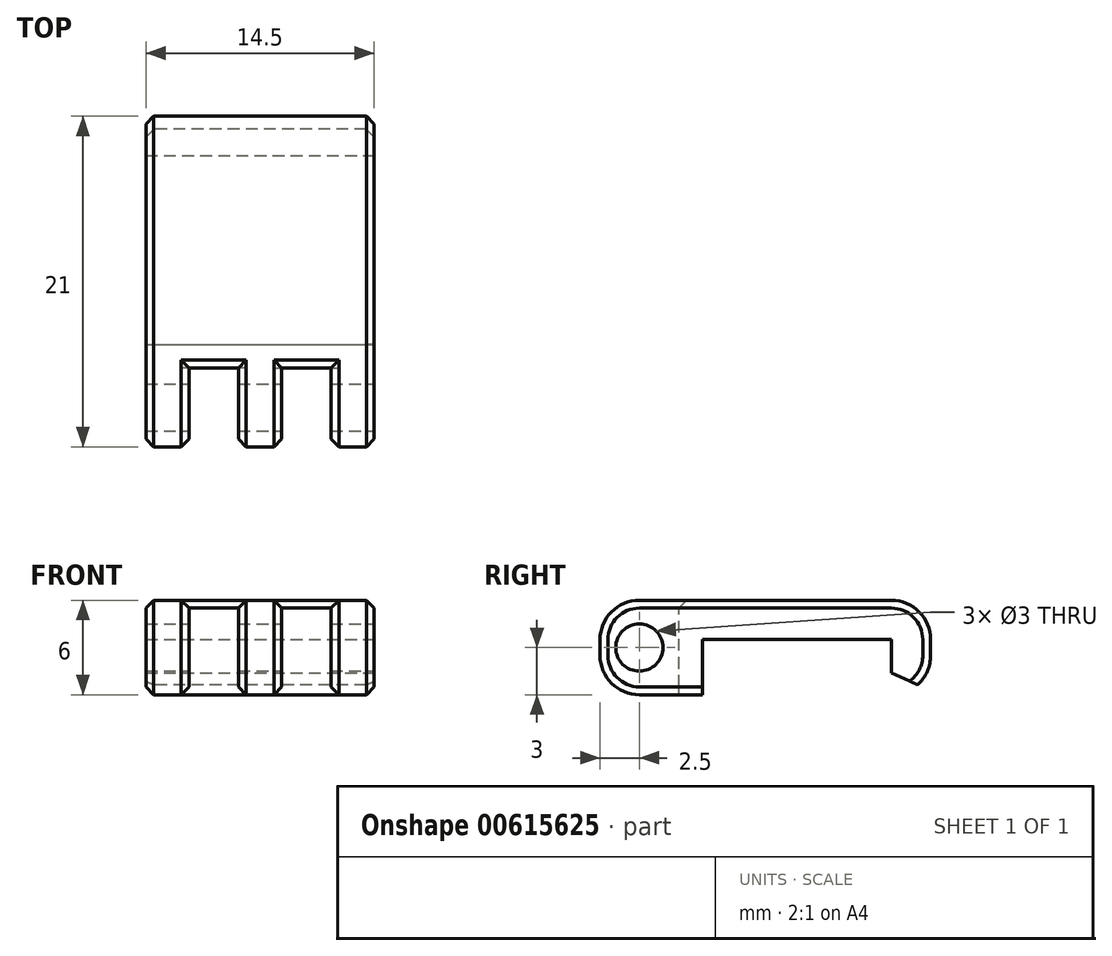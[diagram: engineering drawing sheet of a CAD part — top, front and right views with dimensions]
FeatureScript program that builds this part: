
annotation { "Feature Type Name" : "Feature", "Feature Type Description" : "" }
export const myFeature = defineFeature(function(context is Context, id is Id, definition is map)
    precondition{}
    {
        {
            var Q0;
            Q0=qCreatedBy(makeId("Top.planeOp"),FACE);
            var sketch = newSketch(context, id + "F0", { "sketchPlane" : qUnion([Q0])});
            skLineSegment(sketch, "E0.bottom", {"start": v(-7.25, 10.5) * mm, "end": v(7.25, 10.5) * mm});
            skLineSegment(sketch, "E0.top", {"start": v(-7.25, -10.5) * mm, "end": v(7.25, -10.5) * mm});
            skLineSegment(sketch, "E0.left", {"start": v(-7.25, 10.5) * mm, "end": v(-7.25, -10.5) * mm});
            skLineSegment(sketch, "E0.right", {"start": v(7.25, 10.5) * mm, "end": v(7.25, -10.5) * mm});
            skSolve(sketch);
        }
        {
            var Q0;
            Q0=qSketchRegion(id+"F0",true);
            extrude(context, id + "F1", {"entities" : qUnion([Q0]), "endBound" : BoundingType.SYMMETRIC, "depth" : 6 * mm, "offsetDistance" : 25 * mm});
        }
        {
            var Q0;
            Q0=qCreatedBy(makeId("Right.planeOp"),FACE);
            var sketch = newSketch(context, id + "F2", { "sketchPlane" : qUnion([Q0])});
            skCircle(sketch, "E1", {"center": v(-8, 0) * mm, "radius": 1.5 * mm});
            skSolve(sketch);
        }
        {
            var Q0;
            Q0=qSketchRegion(id+"F2",true);
            extrude(context, id + "F3", {"entities" : qUnion([Q0]), "operationType" : NewBodyOperationType.REMOVE, "endBound" : BoundingType.SYMMETRIC, "oppositeDirection" : true, "depth" : 50 * mm, "offsetDistance" : 25 * mm});
        }
        {
            var Q0;
            Q0=makeQuery(id+"F1.opExtrude","CAP_EDGE",EDGE,{"disambiguationData":[OSD([sQuery(id+"F0.wireOp",EDGE,"E0.top")])],"isStart":false});
            var Q1;
            Q1=makeQuery(id+"F1.opExtrude","CAP_EDGE",EDGE,{"disambiguationData":[OSD([sQuery(id+"F0.wireOp",EDGE,"E0.top")])],"isStart":true});
            var Q2;
            Q2=makeQuery(id+"F1.opExtrude","CAP_EDGE",EDGE,{"disambiguationData":[OSD([sQuery(id+"F0.wireOp",EDGE,"E0.bottom")])],"isStart":false});
            var Q3;
            Q3=makeQuery(id+"F1.opExtrude","CAP_EDGE",EDGE,{"disambiguationData":[OSD([sQuery(id+"F0.wireOp",EDGE,"E0.bottom")])],"isStart":true});
            fillet(context, id + "F4", {"entities" : qUnion([Q0, Q1, Q2, Q3]), "radius" : 2.5 * mm, "tangentPropagation" : true, "allowEdgeOverflow" : false});
        }
        {
            var Q0;
            Q0=qCreatedBy(makeId("Top.planeOp"),FACE);
            var sketch = newSketch(context, id + "F5", { "sketchPlane" : qUnion([Q0])});
            skLineSegment(sketch, "E2", {"start": v(-1.38, -10.5) * mm, "end": v(-4.5, -10.5) * mm});
            skLineSegment(sketch, "E3", {"start": v(-4.5, -10.5) * mm, "end": v(-4.5, -5.5) * mm});
            skLineSegment(sketch, "E4", {"start": v(-4.5, -5.5) * mm, "end": v(-1.37, -5.5) * mm});
            skLineSegment(sketch, "E5", {"start": v(-1.37, -5.5) * mm, "end": v(-1.38, -10.5) * mm});
            skLineSegment(sketch, "E6.MirrorCS", {"start": v(1.38, -10.5) * mm, "end": v(4.5, -10.5) * mm});
            skLineSegment(sketch, "E7.MirrorCS", {"start": v(4.5, -5.5) * mm, "end": v(1.37, -5.5) * mm});
            skLineSegment(sketch, "E8.MirrorCS", {"start": v(1.37, -5.5) * mm, "end": v(1.38, -10.5) * mm});
            skLineSegment(sketch, "E9.MirrorCS", {"start": v(4.5, -10.5) * mm, "end": v(4.5, -5.5) * mm});
            skSolve(sketch);
        }
        {
            var Q0;
            Q0 = qSketchRegion(id + "F5", true);
            extrude(context, id + "F6", {"entities" : qUnion([Q0]), "operationType" : NewBodyOperationType.REMOVE, "endBound" : BoundingType.SYMMETRIC, "oppositeDirection" : true, "depth" : 25 * mm, "offsetDistance" : 25 * mm});
        }
        {
            var Q0;
            Q0=makeQuery(id+"F1.opExtrude","CAP_FACE",FACE,{"disambiguationData":[OSD([sQuery(id+"F0.wireOp",EDGE,"E0.bottom"),sQuery(id+"F0.wireOp",EDGE,"E0.top"),sQuery(id+"F0.wireOp",EDGE,"E0.left"),sQuery(id+"F0.wireOp",EDGE,"E0.right")])],"isStart":true});
            var sketch = newSketch(context, id + "F7", { "sketchPlane" : qUnion([Q0])});
            skLineSegment(sketch, "E10.0", {"start": v(-7.25, -8) * mm, "end": v(-7.25, 4) * mm});
            skLineSegment(sketch, "E11.0", {"start": v(7.25, -8) * mm, "end": v(7.25, 4) * mm});
            skLineSegment(sketch, "E12", {"start": v(-7.25, 4) * mm, "end": v(7.25, 4) * mm});
            skLineSegment(sketch, "E13", {"start": v(7.25, 4) * mm, "end": v(7.25, -8) * mm});
            skPoint(sketch, "E14.orphan", {"position": v(7.25, 8) * mm});
            skPoint(sketch, "E15.orphan", {"position": v(-7.25, 8) * mm});
            skLineSegment(sketch, "E16", {"start": v(7.25, -8) * mm, "end": v(-7.25, -8) * mm});
            skSolve(sketch);
        }
        {
            var Q0;
            Q0 = qSketchRegion(id + "F7", true);
            extrude(context, id + "F8", {"entities" : qUnion([Q0]), "operationType" : NewBodyOperationType.REMOVE, "oppositeDirection" : true, "depth" : 3.5 * mm, "offsetDistance" : 25 * mm});
        }
        {
            var Q0;
            Q0=makeQuery(id+"F8.boolean.opBoolean","COPY",EDGE,{"derivedFrom":makeQuery(id+"F8.opExtrude","CAP_EDGE",EDGE,{"disambiguationData":[OSD([sQuery(id+"F7.wireOp",EDGE,"E12")])],"isStart":true})});
            var Q1;
            {var subQ0=sQuery(id+"F0.wireOp",EDGE,"E0.bottom");Q1=makeQuery(id+"F8.boolean.opBoolean","MERGE",EDGE,{"derivedFrom":[makeQuery(id+"F4.opFillet","BLEND_EDGE",EDGE,{"blendedFrom":[makeQuery(id+"F1.opExtrude","CAP_EDGE",EDGE,{"disambiguationData":[OSD([subQ0])],"isStart":true}),makeQuery(id+"F1.opExtrude","CAP_FACE",FACE,{"disambiguationData":[OSD([subQ0,sQuery(id+"F0.wireOp",EDGE,"E0.top"),sQuery(id+"F0.wireOp",EDGE,"E0.left"),sQuery(id+"F0.wireOp",EDGE,"E0.right")])],"isStart":true})],"blendedInto":[makeQuery(id+"F1.opExtrude","CAP_FACE",FACE,{"disambiguationData":[OSD([subQ0,sQuery(id+"F0.wireOp",EDGE,"E0.top"),sQuery(id+"F0.wireOp",EDGE,"E0.left"),sQuery(id+"F0.wireOp",EDGE,"E0.right")])],"isStart":true})]}),makeQuery(id+"F8.opExtrude","CAP_EDGE",EDGE,{"disambiguationData":[OSD([sQuery(id+"F7.wireOp",EDGE,"E16")])],"isStart":true})]});}
            chamfer(context, id + "F9", {"entities" : qUnion([Q0, Q1]), "width" : 1 * mm, "tangentPropagation" : true});
        }
        {
            var Q0;
            Q0=makeQuery(id+"F1.opExtrude","CAP_EDGE",EDGE,{"disambiguationData":[OSD([sQuery(id+"F0.wireOp",EDGE,"E0.left")])],"isStart":false});
            var Q1;
            Q1=makeQuery(id+"F6.boolean.opBoolean","INTERSECT",EDGE,{"derivedFrom":[makeQuery(id+"F1.opExtrude","CAP_FACE",FACE,{"disambiguationData":[OSD([sQuery(id+"F0.wireOp",EDGE,"E0.bottom"),sQuery(id+"F0.wireOp",EDGE,"E0.top"),sQuery(id+"F0.wireOp",EDGE,"E0.left"),sQuery(id+"F0.wireOp",EDGE,"E0.right")])],"isStart":false}),makeQuery(id+"F6.opExtrude","SWEPT_FACE",FACE,{"disambiguationData":[OSD([sQuery(id+"F5.wireOp",EDGE,"E3")])]})]});
            var Q2;
            Q2=makeQuery(id+"F6.boolean.opBoolean","INTERSECT",EDGE,{"derivedFrom":[makeQuery(id+"F1.opExtrude","CAP_FACE",FACE,{"disambiguationData":[OSD([sQuery(id+"F0.wireOp",EDGE,"E0.bottom"),sQuery(id+"F0.wireOp",EDGE,"E0.top"),sQuery(id+"F0.wireOp",EDGE,"E0.left"),sQuery(id+"F0.wireOp",EDGE,"E0.right")])],"isStart":false}),makeQuery(id+"F6.opExtrude","SWEPT_FACE",FACE,{"disambiguationData":[OSD([sQuery(id+"F5.wireOp",EDGE,"E5")])]})]});
            var Q3;
            Q3=makeQuery(id+"F6.boolean.opBoolean","INTERSECT",EDGE,{"derivedFrom":[makeQuery(id+"F1.opExtrude","CAP_FACE",FACE,{"disambiguationData":[OSD([sQuery(id+"F0.wireOp",EDGE,"E0.bottom"),sQuery(id+"F0.wireOp",EDGE,"E0.top"),sQuery(id+"F0.wireOp",EDGE,"E0.left"),sQuery(id+"F0.wireOp",EDGE,"E0.right")])],"isStart":false}),makeQuery(id+"F6.opExtrude","SWEPT_FACE",FACE,{"disambiguationData":[OSD([sQuery(id+"F5.wireOp",EDGE,"E8.MirrorCS")])]})]});
            var Q4;
            Q4=makeQuery(id+"F6.boolean.opBoolean","INTERSECT",EDGE,{"derivedFrom":[makeQuery(id+"F1.opExtrude","CAP_FACE",FACE,{"disambiguationData":[OSD([sQuery(id+"F0.wireOp",EDGE,"E0.bottom"),sQuery(id+"F0.wireOp",EDGE,"E0.top"),sQuery(id+"F0.wireOp",EDGE,"E0.left"),sQuery(id+"F0.wireOp",EDGE,"E0.right")])],"isStart":false}),makeQuery(id+"F6.opExtrude","SWEPT_FACE",FACE,{"disambiguationData":[OSD([sQuery(id+"F5.wireOp",EDGE,"E9.MirrorCS")])]})]});
            var Q5;
            Q5=makeQuery(id+"F1.opExtrude","CAP_EDGE",EDGE,{"disambiguationData":[OSD([sQuery(id+"F0.wireOp",EDGE,"E0.right")])],"isStart":false});
            var Q6;
            Q6=makeQuery(id+"F6.boolean.opBoolean","INTERSECT",EDGE,{"derivedFrom":[makeQuery(id+"F1.opExtrude","CAP_FACE",FACE,{"disambiguationData":[OSD([sQuery(id+"F0.wireOp",EDGE,"E0.bottom"),sQuery(id+"F0.wireOp",EDGE,"E0.top"),sQuery(id+"F0.wireOp",EDGE,"E0.left"),sQuery(id+"F0.wireOp",EDGE,"E0.right")])],"isStart":false}),makeQuery(id+"F6.opExtrude","SWEPT_FACE",FACE,{"disambiguationData":[OSD([sQuery(id+"F5.wireOp",EDGE,"E7.MirrorCS")])]})]});
            var Q7;
            Q7=makeQuery(id+"F6.boolean.opBoolean","INTERSECT",EDGE,{"derivedFrom":[makeQuery(id+"F1.opExtrude","CAP_FACE",FACE,{"disambiguationData":[OSD([sQuery(id+"F0.wireOp",EDGE,"E0.bottom"),sQuery(id+"F0.wireOp",EDGE,"E0.top"),sQuery(id+"F0.wireOp",EDGE,"E0.left"),sQuery(id+"F0.wireOp",EDGE,"E0.right")])],"isStart":false}),makeQuery(id+"F6.opExtrude","SWEPT_FACE",FACE,{"disambiguationData":[OSD([sQuery(id+"F5.wireOp",EDGE,"E4")])]})]});
            chamfer(context, id + "F10", {"entities" : qUnion([Q0, Q1, Q2, Q3, Q4, Q5, Q6, Q7]), "width" : .5 * mm, "tangentPropagation" : true});
        }
    });
